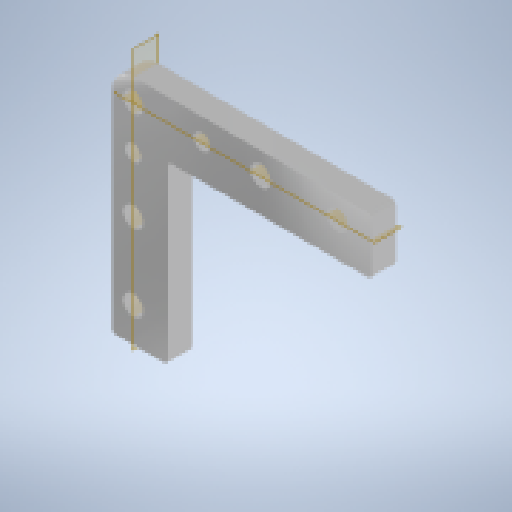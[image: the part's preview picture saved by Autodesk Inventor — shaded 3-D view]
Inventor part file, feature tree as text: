
AUTODESK INVENTOR PART (.ipt)
format: ipt  version: 2024 (Build 280153000, 153)  size: 214,528 bytes
history: native  units: mm
features: other x4, sketch x3, hole x2, fillet x2, plane x2, projected_geometry x2, extrude x1
ambient origin geometry x8: Origin, YZ Plane, XZ Plane, XY Plane, X Axis, Y Axis, Z Axis, Center Point
bodies: Solid1 (feature_tree)
feature tree (16):
  sketch  "Sketch1"  dims[d3=9.0mm d4=9.0mm]
  extrude  "Extrusion1"  Depth=9.0mm
  sketch  "Sketch2"  dims[d5=5.65mm d6=5.65mm d8=8.0mm d9=15.35mm]
  hole  "Hole1"  [1 undecoded]
  fillet  "Fillet1"  Radius=8.0mm
  fillet  "Fillet2"  Radius=15.35mm
  other  "Work Axis1"
  other  "Work Axis2"
  plane  "Work Plane1"
  plane  "Work Plane2"
  hole  "Hole2"  [1 undecoded]
  projected_geometry  "Projected Loop1"
  other  "Work Axis3"
  other  "Work Axis4"
  sketch  "Sketch3"  dims[d11=6.35mm d12=0.0mm d13=5.65mm d14=9.0mm d15=20.0mm d16=5.65mm d17=9.0mm d18=20.0mm d19=5.3mm d20=6.0mm d21=4.0mm d22=2.0mm d23=90.0deg d24=8.0mm d25=20.594885mm d29=1.0mm d30=1.0mm d31=20.0mm d32=20.0mm d33=9.0mm d35=9.0mm d36=11.5mm d37=18.0mm d38=5.2mm d39=6.0mm d40=4.0mm d41=2.0mm d42=90.0deg d43=8.0mm d44=0.0mm]
  projected_geometry  "Projected Loop2"
note: 2 required parameter values undecoded (feature->parameter linkage not recoverable at this tier; creation-order binding heuristic only, values carry confidence <= 0.55)
